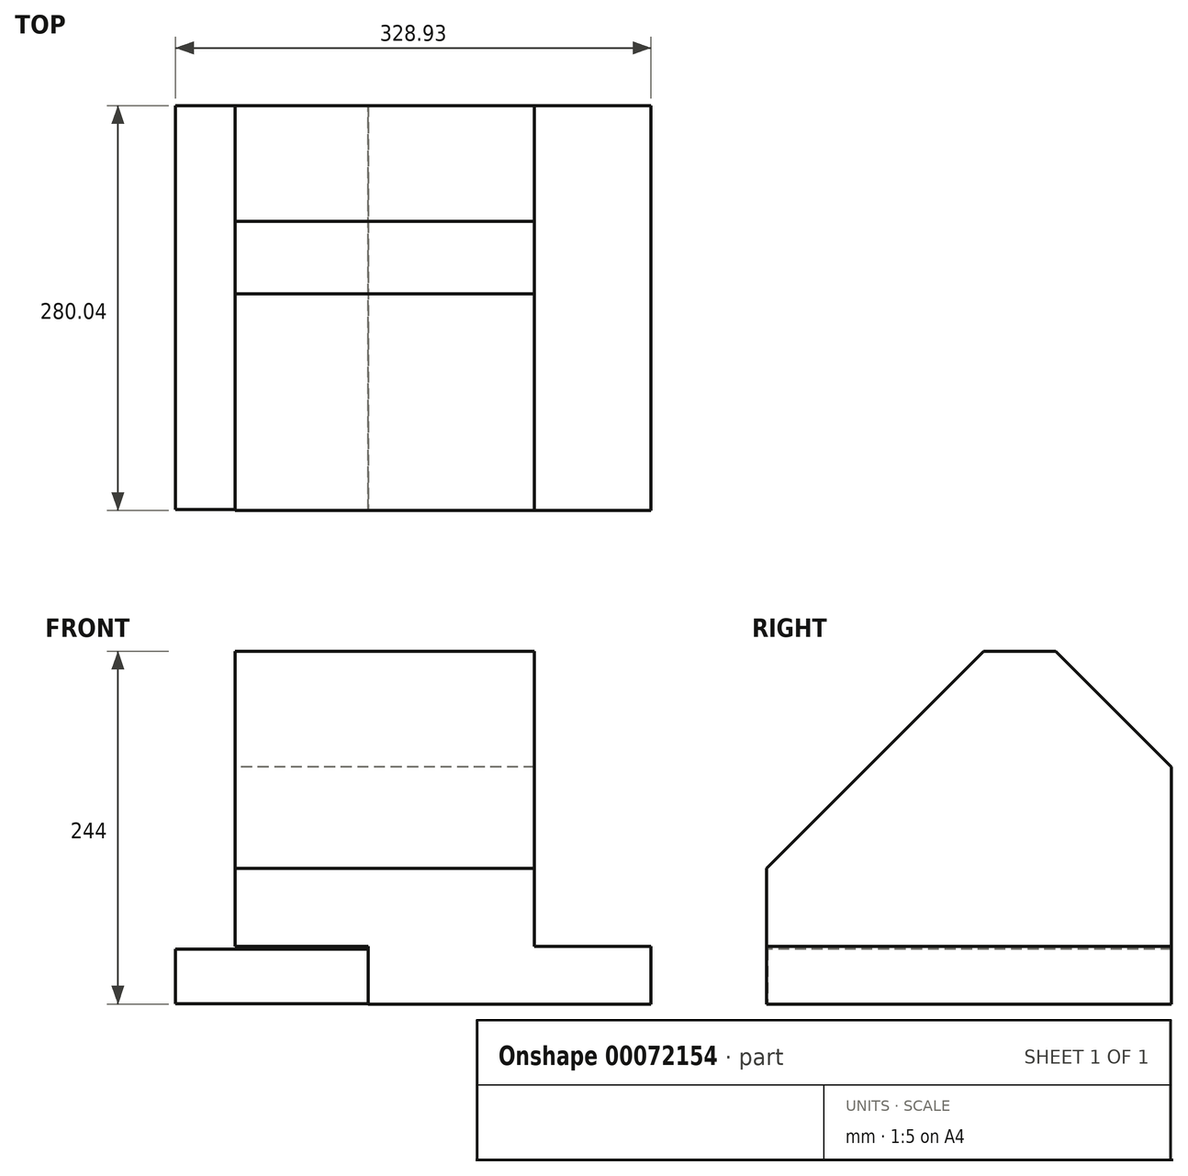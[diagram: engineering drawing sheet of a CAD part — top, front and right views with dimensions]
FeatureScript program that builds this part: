
annotation { "Feature Type Name" : "Feature", "Feature Type Description" : "" }
export const myFeature = defineFeature(function(context is Context, id is Id, definition is map)
    precondition{}
    {
        {
            var Q0;
            Q0=qCreatedBy(makeId("Right.planeOp"),FACE);
            var sketch = newSketch(context, id + "F0", { "sketchPlane" : qUnion([Q0])});
            skLineSegment(sketch, "E0", {"start": v(-129.1, -42.17) * mm, "end": v(150.9, -42.17) * mm});
            skLineSegment(sketch, "E1", {"start": v(-129.1, -42.17) * mm, "end": v(-129.1, 51.83) * mm});
            skLineSegment(sketch, "E2", {"start": v(150.9, -42.17) * mm, "end": v(150.9, 121.83) * mm});
            skLineSegment(sketch, "E3", {"start": v(150.9, 121.83) * mm, "end": v(70.9, 201.83) * mm});
            skLineSegment(sketch, "E4", {"start": v(70.9, 201.83) * mm, "end": v(20.9, 201.83) * mm});
            skLineSegment(sketch, "E5", {"start": v(20.9, 201.83) * mm, "end": v(-129.1, 51.83) * mm});
            skLineSegment(sketch, "E6", {"start": v(-129.1, -2.17) * mm, "end": v(150.9, -2.17) * mm});
            skSolve(sketch);
        }
        {
            var Q0;
            {var subQ0=sQuery(id+"F0.wireOp",EDGE,"E3");Q0=makeQuery(id+"F0.imprint","IMPRINT",FACE,{"disambiguationData":[TD([[makeQuery(id+"F0.imprint","IMPRINT",EDGE,{"derivedFrom":subQ0}),1.0]])]});}
            extrude(context, id + "F1", {"entities" : qUnion([Q0]), "depth" : 114.93 * mm});
        }
        {
            var Q0;
            Q0=qCreatedBy(makeId("Right.planeOp"),FACE);
            var sketch = newSketch(context, id + "F2", { "sketchPlane" : qUnion([Q0])});
            skLineSegment(sketch, "E7", {"start": v(21, 202.3) * mm, "end": v(70.98, 202.3) * mm});
            skLineSegment(sketch, "E8", {"start": v(70.98, 202.3) * mm, "end": v(150.93, 121.72) * mm});
            skLineSegment(sketch, "E9", {"start": v(150.93, 121.72) * mm, "end": v(150.93, -41.9) * mm});
            skLineSegment(sketch, "E10", {"start": v(150.93, -41.9) * mm, "end": v(-128.58, -41.9) * mm});
            skLineSegment(sketch, "E11", {"start": v(-128.58, 52.15) * mm, "end": v(-128.58, -41.9) * mm});
            skLineSegment(sketch, "E12", {"start": v(-128.58, 52.15) * mm, "end": v(21, 202.3) * mm});
            skLineSegment(sketch, "E13", {"start": v(150.93, -4.3) * mm, "end": v(-128.58, -4.3) * mm});
            skSolve(sketch);
        }
        {
            var Q0;
            {var subQ0=sQuery(id+"F0.wireOp",EDGE,"E3");Q0=makeQuery(id+"F0.imprint","IMPRINT",FACE,{"disambiguationData":[TD([[makeQuery(id+"F0.imprint","IMPRINT",EDGE,{"derivedFrom":subQ0}),1.0]])]});}
            extrude(context, id + "F3", {"entities" : qUnion([Q0]), "operationType" : NewBodyOperationType.ADD, "oppositeDirection" : true, "depth" : 92.07 * mm});
        }
        {
            var Q0;
            {var subQ0=sQuery(id+"F0.wireOp",EDGE,"E0");Q0=makeQuery(id+"F0.imprint","IMPRINT",FACE,{"disambiguationData":[TD([[makeQuery(id+"F0.imprint","IMPRINT",EDGE,{"derivedFrom":subQ0}),1.0]])]});}
            extrude(context, id + "F4", {"entities" : qUnion([Q0]), "operationType" : NewBodyOperationType.ADD, "depth" : 195.58 * mm});
        }
        {
            var Q0;
            {var subQ0=sQuery(id+"F2.wireOp",EDGE,"E10");Q0=makeQuery(id+"F2.imprint","IMPRINT",FACE,{"disambiguationData":[TD([[makeQuery(id+"F2.imprint","IMPRINT",EDGE,{"derivedFrom":subQ0}),-1.0]])]});}
            extrude(context, id + "F5", {"entities" : qUnion([Q0]), "operationType" : NewBodyOperationType.ADD, "oppositeDirection" : true, "depth" : 133.35 * mm});
        }
    });
